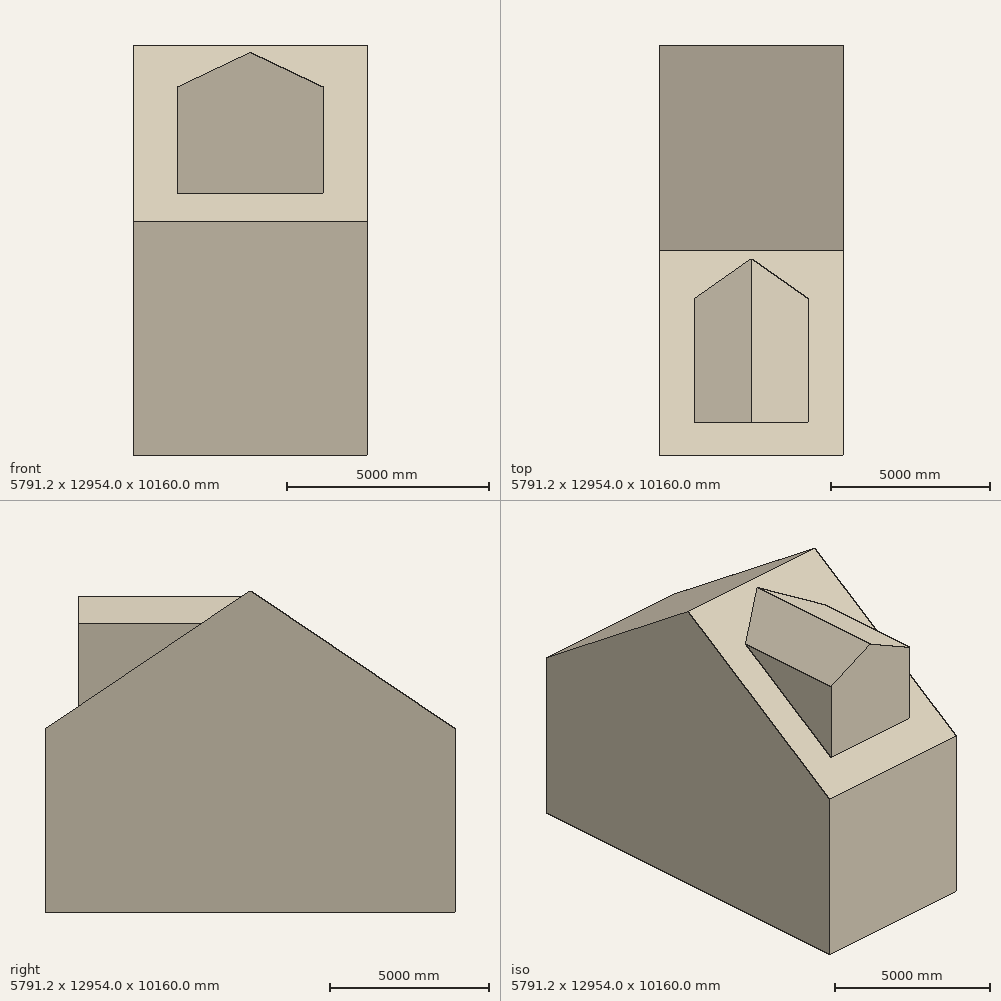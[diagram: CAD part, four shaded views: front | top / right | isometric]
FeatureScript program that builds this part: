
annotation { "Feature Type Name" : "Feature", "Feature Type Description" : "" }
export const myFeature = defineFeature(function(context is Context, id is Id, definition is map)
    precondition{}
    {
        {
            var Q0;
            Q0=qCreatedBy(makeId("Right.planeOp"),FACE);
            var sketch = newSketch(context, id + "F0", { "sketchPlane" : qUnion([Q0])});
            skLineSegment(sketch, "E0.bottom", {"start": v(-6477, -2895.6) * mm, "end": v(6477, -2895.6) * mm});
            skLineSegment(sketch, "E0.top", {"start": v(-6477, 2895.6) * mm, "end": v(6477, 2895.6) * mm});
            skLineSegment(sketch, "E0.left", {"start": v(-6477, -2895.6) * mm, "end": v(-6477, 2895.6) * mm});
            skLineSegment(sketch, "E0.right", {"start": v(6477, -2895.6) * mm, "end": v(6477, 2895.6) * mm});
            skPoint(sketch, "E0.middle", {"position": v(0, 0) * mm});
            skLineSegment(sketch, "E1", {"start": v(-6477, 2895.6) * mm, "end": v(0, 7264.4) * mm});
            skLineSegment(sketch, "E2", {"start": v(0, 7264.4) * mm, "end": v(6477, 2895.6) * mm});
            skSolve(sketch);
        }
        {
            var Q0;
            Q0=makeQuery(id+"F0.imprint","IMPRINT",FACE,{"disambiguationData":[TD([[makeQuery(id+"F0.imprint","IMPRINT",EDGE,{"derivedFrom":sQuery(id+"F0.wireOp",EDGE,"E0.bottom")}),1.0]])]});
            var Q1;
            Q1=makeQuery(id+"F0.imprint","IMPRINT",FACE,{"disambiguationData":[TD([[makeQuery(id+"F0.imprint","IMPRINT",EDGE,{"derivedFrom":sQuery(id+"F0.wireOp",EDGE,"E0.top")}),1.0]])]});
            extrude(context, id + "F1", {"entities" : qUnion([Q0, Q1]), "endBound" : BoundingType.SYMMETRIC, "depth" : 5791.2 * mm});
        }
        {
            var Q0;
            Q0=qCreatedBy(makeId("Front.planeOp"),FACE);
            var sketch = newSketch(context, id + "F2", { "sketchPlane" : qUnion([Q0])});
            skLineSegment(sketch, "E3.bottom", {"start": v(1803.47, 2300.35) * mm, "end": v(-1803.47, 2300.35) * mm});
            skLineSegment(sketch, "E3.top", {"start": v(1803.47, 6232.76) * mm, "end": v(-1803.47, 6232.76) * mm});
            skLineSegment(sketch, "E3.left", {"start": v(1803.47, 2300.35) * mm, "end": v(1803.47, 6232.76) * mm});
            skLineSegment(sketch, "E3.right", {"start": v(-1803.47, 2300.35) * mm, "end": v(-1803.47, 6232.76) * mm});
            skPoint(sketch, "E3.middle", {"position": v(0, 4266.56) * mm});
            skLineSegment(sketch, "E4", {"start": v(-1803.47, 6232.76) * mm, "end": v(0, 7090.42) * mm});
            skLineSegment(sketch, "E5", {"start": v(0, 7090.42) * mm, "end": v(1803.47, 6232.76) * mm});
            skSolve(sketch);
        }
        {
            var Q0;
            Q0 = qSketchRegion(id + "F2", true);
            extrude(context, id + "F3", {"entities" : qUnion([Q0]), "operationType" : NewBodyOperationType.ADD, "depth" : 5440 * mm});
        }
    });
